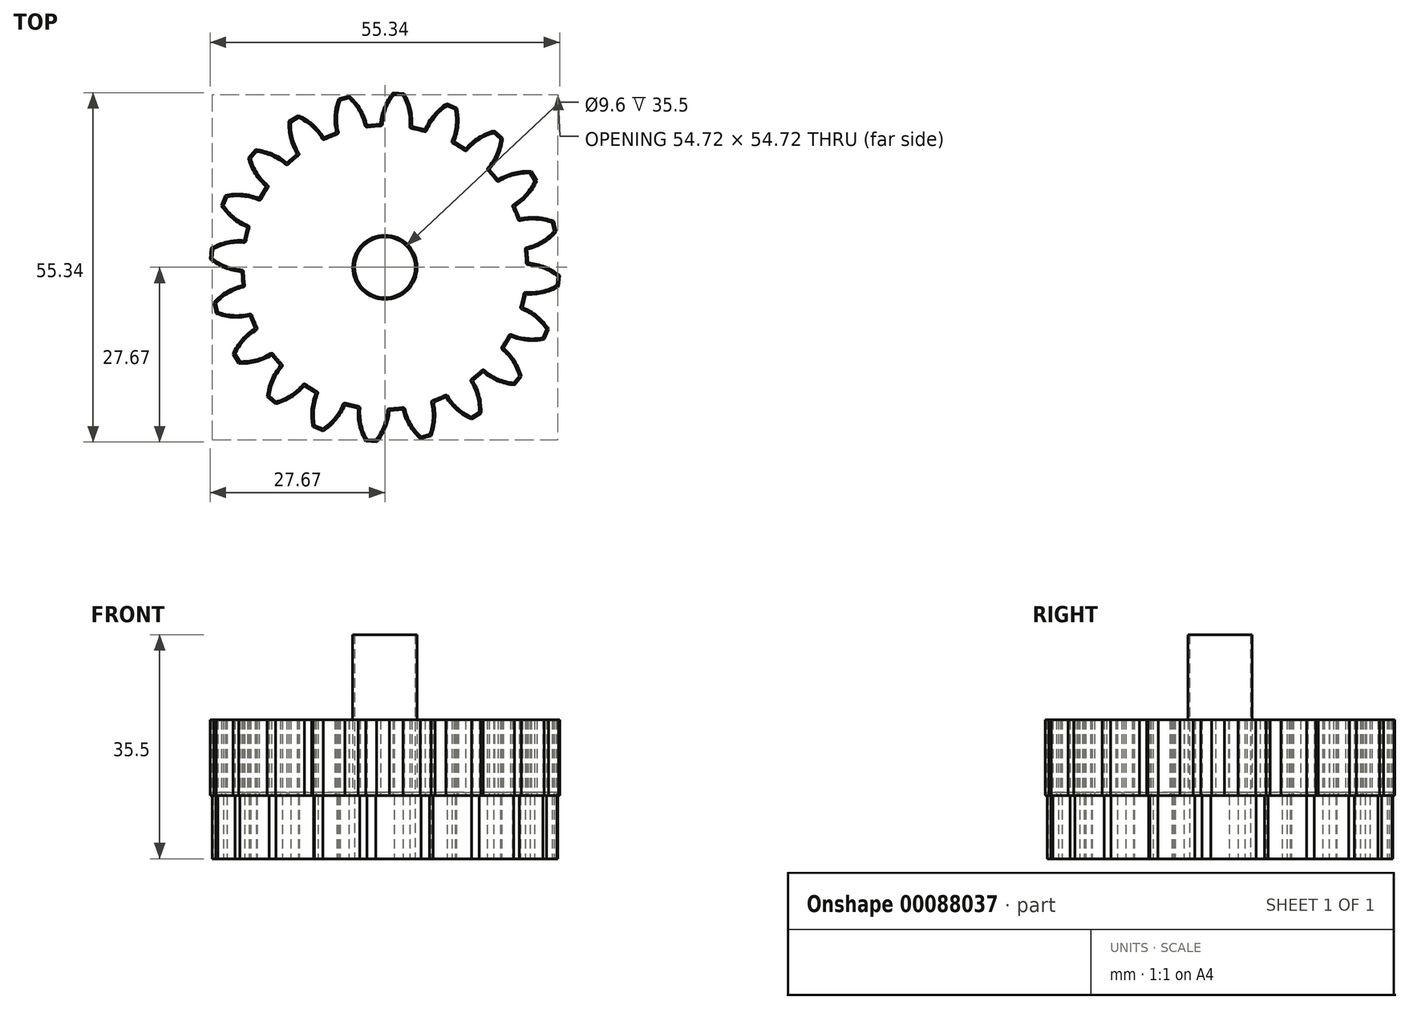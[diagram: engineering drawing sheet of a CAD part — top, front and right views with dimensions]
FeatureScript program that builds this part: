
annotation { "Feature Type Name" : "Feature", "Feature Type Description" : "" }
export const myFeature = defineFeature(function(context is Context, id is Id, definition is map)
    precondition{}
    {
        {
            assignVariable(context, id + "F0", {"name" : "z", "anyValue" : 20});
        }
        {
            assignVariable(context, id + "F1", {"name" : "b1", "anyValue" : 10});
        }
        {
            var Q0;
            Q0=qCreatedBy(makeId("Top.planeOp"),FACE);
            var sketch = newSketch(context, id + "F2", { "sketchPlane" : qUnion([Q0])});
            skCircle(sketch, "E0", {"center": v(0, 0) * mm, "radius": 27.5 * mm, "construction": true});
            skCircle(sketch, "E1", {"center": v(0, 0) * mm, "radius": 23.5 * mm, "construction": true});
            skCircle(sketch, "E2", {"center": v(0, 0) * mm, "radius": 25 * mm, "construction": true});
            skCircle(sketch, "E3", {"center": v(0, 0) * mm, "radius": 22.5 * mm, "construction": true});
            skLineSegment(sketch, "E4", {"start": v(0, 0) * mm, "end": v(9.4, 25.84) * mm, "construction": true});
            skLineSegment(sketch, "E5", {"start": v(0, 27.5) * mm, "end": v(0, 0) * mm, "construction": true});
            skCircle(sketch, "E6", {"center": v(8.03, 22.08) * mm, "radius": 8.55 * mm, "construction": true});
            skPoint(sketch, "E7", {"position": v(0, 25) * mm});
            skLineSegment(sketch, "E8", {"start": v(4.3, 27.16) * mm, "end": v(0, 0) * mm, "construction": true});
            skLineSegment(sketch, "E9", {"start": v(0, 0) * mm, "end": v(-5.25, 27) * mm, "construction": true});
            skCircle(sketch, "E10", {"center": v(-4.48, 23.06) * mm, "radius": 8.55 * mm, "construction": true});
            skPoint(sketch, "E11", {"position": v(3.91, 24.7) * mm});
            skCircle(sketch, "E12", {"center": v(0, 0) * mm, "radius": 22.4 * mm, "construction": true});
            skCircle(sketch, "E13", {"center": v(0, 0) * mm, "radius": 27.4 * mm, "construction": true});
            skCircle(sketch, "E14", {"center": v(-4.48, 23.06) * mm, "radius": 8.45 * mm, "construction": true});
            skCircle(sketch, "E15", {"center": v(8.03, 22.08) * mm, "radius": 8.45 * mm, "construction": true});
            skCircle(sketch, "E16", {"center": v(-0.7, 22.69) * mm, "radius": 0.3 * mm, "construction": true});
            skCircle(sketch, "E17", {"center": v(4.23, 22.3) * mm, "radius": 0.3 * mm, "construction": true});
            skPoint(sketch, "E18", {"position": v(-0.68, 22.39) * mm});
            skPoint(sketch, "E19", {"position": v(-0.4, 22.67) * mm});
            skPoint(sketch, "E20", {"position": v(3.94, 22.33) * mm});
            skPoint(sketch, "E21", {"position": v(4.18, 22) * mm});
            skPoint(sketch, "E22", {"position": v(2.86, 27.25) * mm});
            skPoint(sketch, "E23", {"position": v(1.44, 27.36) * mm});
            skArc(sketch, "E24", {"start": v(-0.68, 22.39) * mm, "mid": v(-0.49, 22.47) * mm, "end": v(-0.4, 22.67) * mm});
            skArc(sketch, "E25", {"start": v(1.44, 27.36) * mm, "mid": v(0.17, 25.16) * mm, "end": v(-0.4, 22.67) * mm});
            skArc(sketch, "E26", {"start": v(3.94, 22.33) * mm, "mid": v(4, 22.12) * mm, "end": v(4.18, 22) * mm});
            skArc(sketch, "E27", {"start": v(3.94, 22.33) * mm, "mid": v(3.77, 24.87) * mm, "end": v(2.86, 27.25) * mm});
            skArc(sketch, "E28", {"start": v(4.18, 22) * mm, "mid": v(1.76, 22.33) * mm, "end": v(-0.68, 22.39) * mm});
            skLineSegment(sketch, "E29", {"start": v(2.86, 27.25) * mm, "end": v(1.44, 27.36) * mm});
            skSolve(sketch);
        }
        {
            var Q0;
            Q0=qSketchRegion(id+"F2",true);
            extrude(context, id + "F3", {"entities" : qUnion([Q0]), "depth" : (getVariable(context, 'b1')) * mm});
        }
        {
            var Q0;
            Q0=qCreatedBy(makeId("Front.planeOp"),FACE);
            var sketch = newSketch(context, id + "F4", { "sketchPlane" : qUnion([Q0])});
            skLineSegment(sketch, "E30", {"start": v(0, 0) * mm, "end": v(0, 15) * mm, "construction": true});
            skSolve(sketch);
        }
        {
            var Q0;
            Q0=makeQuery(id+"F3.opExtrude","SWEPT_BODY",BODY,{"disambiguationData":[OSD([sQuery(id+"F2.wireOp",EDGE,"E24"),sQuery(id+"F2.wireOp",EDGE,"E25"),sQuery(id+"F2.wireOp",EDGE,"E26"),sQuery(id+"F2.wireOp",EDGE,"E27"),sQuery(id+"F2.wireOp",EDGE,"E28"),sQuery(id+"F2.wireOp",EDGE,"debd62c7-c6de-4254-9725-9acab07f6eeb")])]});
            var Q1;
            Q1=sQuery(id+"F4.wireOp",EDGE,"E30");
            circularPattern(context, id + "F5", {"entities" : qUnion([Q0]), "axis" : qUnion([Q1]), "angle" : (360 / getVariable(context, 'z')) * degree, "instanceCount" : getVariable(context, 'z')});
        }
        {
            var Q0;
            Q0=qCreatedBy(makeId("Top.planeOp"),FACE);
            var sketch = newSketch(context, id + "F6", { "sketchPlane" : qUnion([Q0])});
            skCircle(sketch, "E31", {"center": v(0, 0) * mm, "radius": 22.4 * mm});
            skCircle(sketch, "E32", {"center": v(0, 0) * mm, "radius": 4.8 * mm});
            skSolve(sketch);
        }
        {
            var Q0;
            Q0=qSketchRegion(id+"F6",true);
            extrude(context, id + "F7", {"entities" : qUnion([Q0]), "operationType" : NewBodyOperationType.ADD, "depth" : (getVariable(context, 'b1')) * mm});
        }
        {
            var Q0;
            {var subQ0=makeQuery(id+"F3.opExtrude","CAP_FACE",FACE,{"disambiguationData":[OSD([sQuery(id+"F2.wireOp",EDGE,"E24"),sQuery(id+"F2.wireOp",EDGE,"E25"),sQuery(id+"F2.wireOp",EDGE,"E26"),sQuery(id+"F2.wireOp",EDGE,"E27"),sQuery(id+"F2.wireOp",EDGE,"E28"),sQuery(id+"F2.wireOp",EDGE,"E29")])],"isStart":false});Q0=makeQuery(id+"F7.boolean.opBoolean","MERGE",FACE,{"derivedFrom":[subQ0,makeQuery(id+"F5.opPattern","COPY",FACE,{"derivedFrom":subQ0,"instanceName":"1"}),makeQuery(id+"F5.opPattern","COPY",FACE,{"derivedFrom":subQ0,"instanceName":"2"}),makeQuery(id+"F5.opPattern","COPY",FACE,{"derivedFrom":subQ0,"instanceName":"3"}),makeQuery(id+"F5.opPattern","COPY",FACE,{"derivedFrom":subQ0,"instanceName":"4"}),makeQuery(id+"F5.opPattern","COPY",FACE,{"derivedFrom":subQ0,"instanceName":"5"}),makeQuery(id+"F5.opPattern","COPY",FACE,{"derivedFrom":subQ0,"instanceName":"6"}),makeQuery(id+"F5.opPattern","COPY",FACE,{"derivedFrom":subQ0,"instanceName":"7"}),makeQuery(id+"F5.opPattern","COPY",FACE,{"derivedFrom":subQ0,"instanceName":"8"}),makeQuery(id+"F5.opPattern","COPY",FACE,{"derivedFrom":subQ0,"instanceName":"9"}),makeQuery(id+"F5.opPattern","COPY",FACE,{"derivedFrom":subQ0,"instanceName":"10"}),makeQuery(id+"F5.opPattern","COPY",FACE,{"derivedFrom":subQ0,"instanceName":"11"}),makeQuery(id+"F5.opPattern","COPY",FACE,{"derivedFrom":subQ0,"instanceName":"12"}),makeQuery(id+"F5.opPattern","COPY",FACE,{"derivedFrom":subQ0,"instanceName":"13"}),makeQuery(id+"F5.opPattern","COPY",FACE,{"derivedFrom":subQ0,"instanceName":"14"}),makeQuery(id+"F5.opPattern","COPY",FACE,{"derivedFrom":subQ0,"instanceName":"15"}),makeQuery(id+"F5.opPattern","COPY",FACE,{"derivedFrom":subQ0,"instanceName":"16"}),makeQuery(id+"F5.opPattern","COPY",FACE,{"derivedFrom":subQ0,"instanceName":"17"}),makeQuery(id+"F5.opPattern","COPY",FACE,{"derivedFrom":subQ0,"instanceName":"18"}),makeQuery(id+"F5.opPattern","COPY",FACE,{"derivedFrom":subQ0,"instanceName":"19"}),makeQuery(id+"F7.opExtrude","CAP_FACE",FACE,{"disambiguationData":[OSD([sQuery(id+"F6.wireOp",EDGE,"E31"),sQuery(id+"F6.wireOp",EDGE,"E32")])],"isStart":false})]});}
            var sketch = newSketch(context, id + "F8", { "sketchPlane" : qUnion([Q0])});
            skArc(sketch, "E33.0", {"start": v(1.44, 27.36) * mm, "mid": v(0.17, 25.16) * mm, "end": v(-0.4, 22.67) * mm});
            skLineSegment(sketch, "E33.1", {"start": v(2.86, 27.25) * mm, "end": v(1.44, 27.36) * mm});
            skArc(sketch, "E33.2", {"start": v(3.94, 22.33) * mm, "mid": v(3.77, 24.87) * mm, "end": v(2.86, 27.25) * mm});
            skArc(sketch, "E33.3", {"start": v(-0.68, 22.39) * mm, "mid": v(-0.49, 22.47) * mm, "end": v(-0.4, 22.67) * mm});
            skArc(sketch, "E33.4", {"start": v(3.94, 22.33) * mm, "mid": v(4, 22.12) * mm, "end": v(4.18, 22) * mm});
            skArc(sketch, "E33.5", {"start": v(6.27, 21.5) * mm, "mid": v(5.23, 21.78) * mm, "end": v(4.18, 22) * mm});
            skArc(sketch, "E34", {"start": v(1.3, 27.67) * mm, "mid": v(-0.08, 25.34) * mm, "end": v(-0.7, 22.69) * mm});
            skArc(sketch, "E35", {"start": v(4.23, 22.3) * mm, "mid": v(4.05, 25.01) * mm, "end": v(3.04, 27.54) * mm});
            skLineSegment(sketch, "E36", {"start": v(1.3, 27.67) * mm, "end": v(3.04, 27.54) * mm});
            skArc(sketch, "E37.0", {"start": v(6.27, 21.5) * mm, "mid": v(6.48, 21.52) * mm, "end": v(6.63, 21.68) * mm, "construction": true});
            skLineSegment(sketch, "E38", {"start": v(4.23, 22.3) * mm, "end": v(6.35, 21.8) * mm});
            skArc(sketch, "E39.1.0", {"start": v(-2.86, 22.52) * mm, "mid": v(-3.88, 25.04) * mm, "end": v(-5.62, 27.13) * mm});
            skArc(sketch, "E39.1.1", {"start": v(-7.3, 26.72) * mm, "mid": v(-7.91, 24.07) * mm, "end": v(-7.67, 21.36) * mm});
            skArc(sketch, "E39.1.2", {"start": v(-0.68, 22.39) * mm, "mid": v(-1.76, 22.33) * mm, "end": v(-2.83, 22.22) * mm});
            skArc(sketch, "E39.1.3", {"start": v(-3.16, 22.45) * mm, "mid": v(-4.1, 24.82) * mm, "end": v(-5.7, 26.8) * mm});
            skLineSegment(sketch, "E39.1.4", {"start": v(-5.7, 26.8) * mm, "end": v(-7.08, 26.47) * mm});
            skArc(sketch, "E39.1.5", {"start": v(-7.08, 26.47) * mm, "mid": v(-7.62, 23.98) * mm, "end": v(-7.38, 21.44) * mm});
            skLineSegment(sketch, "E39.1.6", {"start": v(-7.3, 26.72) * mm, "end": v(-5.62, 27.13) * mm});
            skLineSegment(sketch, "E39.1.7", {"start": v(-2.86, 22.52) * mm, "end": v(-0.7, 22.69) * mm});
            skArc(sketch, "E39.1.8", {"start": v(-7.57, 21.08) * mm, "mid": v(-7.4, 21.22) * mm, "end": v(-7.38, 21.44) * mm});
            skArc(sketch, "E39.1.9", {"start": v(-3.16, 22.45) * mm, "mid": v(-3.04, 22.27) * mm, "end": v(-2.83, 22.22) * mm});
            skArc(sketch, "E39.2.0", {"start": v(-9.68, 20.53) * mm, "mid": v(-11.43, 22.62) * mm, "end": v(-13.73, 24.06) * mm});
            skArc(sketch, "E39.2.1", {"start": v(-15.2, 23.16) * mm, "mid": v(-14.96, 20.45) * mm, "end": v(-13.9, 17.95) * mm});
            skArc(sketch, "E39.2.2", {"start": v(-7.57, 21.08) * mm, "mid": v(-8.57, 20.7) * mm, "end": v(-9.55, 20.26) * mm});
            skArc(sketch, "E39.2.3", {"start": v(-9.94, 20.38) * mm, "mid": v(-11.57, 22.34) * mm, "end": v(-13.7, 23.73) * mm});
            skLineSegment(sketch, "E39.2.4", {"start": v(-13.7, 23.73) * mm, "end": v(-14.92, 22.98) * mm});
            skArc(sketch, "E39.2.5", {"start": v(-14.92, 22.98) * mm, "mid": v(-14.65, 20.45) * mm, "end": v(-13.64, 18.1) * mm});
            skLineSegment(sketch, "E39.2.6", {"start": v(-15.2, 23.16) * mm, "end": v(-13.73, 24.06) * mm});
            skLineSegment(sketch, "E39.2.7", {"start": v(-9.68, 20.53) * mm, "end": v(-7.67, 21.36) * mm});
            skArc(sketch, "E39.2.8", {"start": v(-13.71, 17.71) * mm, "mid": v(-13.6, 17.9) * mm, "end": v(-13.64, 18.1) * mm});
            skArc(sketch, "E39.2.9", {"start": v(-9.94, 20.38) * mm, "mid": v(-9.77, 20.24) * mm, "end": v(-9.55, 20.26) * mm});
            skArc(sketch, "E39.3.0", {"start": v(-15.55, 16.53) * mm, "mid": v(-17.86, 17.98) * mm, "end": v(-20.5, 18.64) * mm});
            skArc(sketch, "E39.3.1", {"start": v(-21.62, 17.33) * mm, "mid": v(-20.55, 14.83) * mm, "end": v(-18.76, 12.77) * mm});
            skArc(sketch, "E39.3.2", {"start": v(-13.71, 17.71) * mm, "mid": v(-14.55, 17.03) * mm, "end": v(-15.35, 16.32) * mm});
            skArc(sketch, "E39.3.3", {"start": v(-15.75, 16.3) * mm, "mid": v(-17.9, 17.67) * mm, "end": v(-20.37, 18.33) * mm});
            skLineSegment(sketch, "E39.3.4", {"start": v(-20.37, 18.33) * mm, "end": v(-21.29, 17.25) * mm});
            skArc(sketch, "E39.3.5", {"start": v(-21.29, 17.25) * mm, "mid": v(-20.25, 14.92) * mm, "end": v(-18.57, 13) * mm});
            skLineSegment(sketch, "E39.3.6", {"start": v(-21.62, 17.33) * mm, "end": v(-20.5, 18.64) * mm});
            skLineSegment(sketch, "E39.3.7", {"start": v(-15.55, 16.53) * mm, "end": v(-13.9, 17.95) * mm});
            skArc(sketch, "E39.3.8", {"start": v(-18.52, 12.6) * mm, "mid": v(-18.47, 12.82) * mm, "end": v(-18.57, 13) * mm});
            skArc(sketch, "E39.3.9", {"start": v(-15.75, 16.3) * mm, "mid": v(-15.55, 16.23) * mm, "end": v(-15.35, 16.32) * mm});
            skArc(sketch, "E39.4.0", {"start": v(-19.9, 10.92) * mm, "mid": v(-22.54, 11.58) * mm, "end": v(-25.25, 11.4) * mm});
            skArc(sketch, "E39.4.1", {"start": v(-25.91, 9.8) * mm, "mid": v(-24.12, 7.75) * mm, "end": v(-21.8, 6.35) * mm});
            skArc(sketch, "E39.4.2", {"start": v(-18.52, 12.6) * mm, "mid": v(-19.1, 11.7) * mm, "end": v(-19.64, 10.77) * mm});
            skArc(sketch, "E39.4.3", {"start": v(-20.02, 10.64) * mm, "mid": v(-22.49, 11.27) * mm, "end": v(-25.03, 11.14) * mm});
            skLineSegment(sketch, "E39.4.4", {"start": v(-25.03, 11.14) * mm, "end": v(-25.58, 9.83) * mm});
            skArc(sketch, "E39.4.5", {"start": v(-25.58, 9.83) * mm, "mid": v(-23.87, 7.93) * mm, "end": v(-21.68, 6.63) * mm});
            skLineSegment(sketch, "E39.4.6", {"start": v(-25.91, 9.8) * mm, "end": v(-25.25, 11.4) * mm});
            skLineSegment(sketch, "E39.4.7", {"start": v(-19.9, 10.92) * mm, "end": v(-18.76, 12.77) * mm});
            skArc(sketch, "E39.4.8", {"start": v(-21.5, 6.27) * mm, "mid": v(-21.52, 6.48) * mm, "end": v(-21.68, 6.63) * mm});
            skArc(sketch, "E39.4.9", {"start": v(-20.02, 10.64) * mm, "mid": v(-19.8, 10.64) * mm, "end": v(-19.64, 10.77) * mm});
            skArc(sketch, "E39.5.0", {"start": v(-22.3, 4.23) * mm, "mid": v(-25.01, 4.05) * mm, "end": v(-27.54, 3.04) * mm});
            skArc(sketch, "E39.5.1", {"start": v(-27.67, 1.3) * mm, "mid": v(-25.34, -0.08) * mm, "end": v(-22.69, -0.7) * mm});
            skArc(sketch, "E39.5.2", {"start": v(-21.5, 6.27) * mm, "mid": v(-21.78, 5.23) * mm, "end": v(-22, 4.18) * mm});
            skArc(sketch, "E39.5.3", {"start": v(-22.33, 3.94) * mm, "mid": v(-24.87, 3.77) * mm, "end": v(-27.25, 2.86) * mm});
            skLineSegment(sketch, "E39.5.4", {"start": v(-27.25, 2.86) * mm, "end": v(-27.36, 1.44) * mm});
            skArc(sketch, "E39.5.5", {"start": v(-27.36, 1.44) * mm, "mid": v(-25.16, 0.17) * mm, "end": v(-22.67, -0.4) * mm});
            skLineSegment(sketch, "E39.5.6", {"start": v(-27.67, 1.3) * mm, "end": v(-27.54, 3.04) * mm});
            skLineSegment(sketch, "E39.5.7", {"start": v(-22.3, 4.23) * mm, "end": v(-21.8, 6.35) * mm});
            skArc(sketch, "E39.5.8", {"start": v(-22.39, -0.68) * mm, "mid": v(-22.47, -0.49) * mm, "end": v(-22.67, -0.4) * mm});
            skArc(sketch, "E39.5.9", {"start": v(-22.33, 3.94) * mm, "mid": v(-22.12, 4) * mm, "end": v(-22, 4.18) * mm});
            skArc(sketch, "E39.6.0", {"start": v(-22.52, -2.86) * mm, "mid": v(-25.04, -3.88) * mm, "end": v(-27.13, -5.62) * mm});
            skArc(sketch, "E39.6.1", {"start": v(-26.72, -7.3) * mm, "mid": v(-24.07, -7.91) * mm, "end": v(-21.36, -7.67) * mm});
            skArc(sketch, "E39.6.2", {"start": v(-22.39, -0.68) * mm, "mid": v(-22.33, -1.76) * mm, "end": v(-22.22, -2.83) * mm});
            skArc(sketch, "E39.6.3", {"start": v(-22.45, -3.16) * mm, "mid": v(-24.82, -4.1) * mm, "end": v(-26.8, -5.7) * mm});
            skLineSegment(sketch, "E39.6.4", {"start": v(-26.8, -5.7) * mm, "end": v(-26.47, -7.08) * mm});
            skArc(sketch, "E39.6.5", {"start": v(-26.47, -7.08) * mm, "mid": v(-23.98, -7.62) * mm, "end": v(-21.44, -7.38) * mm});
            skLineSegment(sketch, "E39.6.6", {"start": v(-26.72, -7.3) * mm, "end": v(-27.13, -5.62) * mm});
            skLineSegment(sketch, "E39.6.7", {"start": v(-22.52, -2.86) * mm, "end": v(-22.69, -0.7) * mm});
            skArc(sketch, "E39.6.8", {"start": v(-21.08, -7.57) * mm, "mid": v(-21.22, -7.4) * mm, "end": v(-21.44, -7.38) * mm});
            skArc(sketch, "E39.6.9", {"start": v(-22.45, -3.16) * mm, "mid": v(-22.27, -3.04) * mm, "end": v(-22.22, -2.83) * mm});
            skArc(sketch, "E39.7.0", {"start": v(-20.53, -9.68) * mm, "mid": v(-22.62, -11.43) * mm, "end": v(-24.06, -13.73) * mm});
            skArc(sketch, "E39.7.1", {"start": v(-23.16, -15.2) * mm, "mid": v(-20.45, -14.96) * mm, "end": v(-17.95, -13.9) * mm});
            skArc(sketch, "E39.7.2", {"start": v(-21.08, -7.57) * mm, "mid": v(-20.7, -8.57) * mm, "end": v(-20.26, -9.55) * mm});
            skArc(sketch, "E39.7.3", {"start": v(-20.38, -9.94) * mm, "mid": v(-22.34, -11.57) * mm, "end": v(-23.73, -13.7) * mm});
            skLineSegment(sketch, "E39.7.4", {"start": v(-23.73, -13.7) * mm, "end": v(-22.98, -14.92) * mm});
            skArc(sketch, "E39.7.5", {"start": v(-22.98, -14.92) * mm, "mid": v(-20.45, -14.65) * mm, "end": v(-18.1, -13.64) * mm});
            skLineSegment(sketch, "E39.7.6", {"start": v(-23.16, -15.2) * mm, "end": v(-24.06, -13.73) * mm});
            skLineSegment(sketch, "E39.7.7", {"start": v(-20.53, -9.68) * mm, "end": v(-21.36, -7.67) * mm});
            skArc(sketch, "E39.7.8", {"start": v(-17.71, -13.71) * mm, "mid": v(-17.9, -13.6) * mm, "end": v(-18.1, -13.64) * mm});
            skArc(sketch, "E39.7.9", {"start": v(-20.38, -9.94) * mm, "mid": v(-20.24, -9.77) * mm, "end": v(-20.26, -9.55) * mm});
            skArc(sketch, "E39.8.0", {"start": v(-16.53, -15.55) * mm, "mid": v(-17.98, -17.86) * mm, "end": v(-18.64, -20.5) * mm});
            skArc(sketch, "E39.8.1", {"start": v(-17.33, -21.62) * mm, "mid": v(-14.83, -20.55) * mm, "end": v(-12.77, -18.76) * mm});
            skArc(sketch, "E39.8.2", {"start": v(-17.71, -13.71) * mm, "mid": v(-17.03, -14.55) * mm, "end": v(-16.32, -15.35) * mm});
            skArc(sketch, "E39.8.3", {"start": v(-16.3, -15.75) * mm, "mid": v(-17.67, -17.9) * mm, "end": v(-18.33, -20.37) * mm});
            skLineSegment(sketch, "E39.8.4", {"start": v(-18.33, -20.37) * mm, "end": v(-17.25, -21.29) * mm});
            skArc(sketch, "E39.8.5", {"start": v(-17.25, -21.29) * mm, "mid": v(-14.92, -20.25) * mm, "end": v(-13, -18.57) * mm});
            skLineSegment(sketch, "E39.8.6", {"start": v(-17.33, -21.62) * mm, "end": v(-18.64, -20.5) * mm});
            skLineSegment(sketch, "E39.8.7", {"start": v(-16.53, -15.55) * mm, "end": v(-17.95, -13.9) * mm});
            skArc(sketch, "E39.8.8", {"start": v(-12.6, -18.52) * mm, "mid": v(-12.82, -18.47) * mm, "end": v(-13, -18.57) * mm});
            skArc(sketch, "E39.8.9", {"start": v(-16.3, -15.75) * mm, "mid": v(-16.23, -15.55) * mm, "end": v(-16.32, -15.35) * mm});
            skArc(sketch, "E39.9.0", {"start": v(-10.92, -19.9) * mm, "mid": v(-11.58, -22.54) * mm, "end": v(-11.4, -25.25) * mm});
            skArc(sketch, "E39.9.1", {"start": v(-9.8, -25.91) * mm, "mid": v(-7.75, -24.12) * mm, "end": v(-6.35, -21.8) * mm});
            skArc(sketch, "E39.9.2", {"start": v(-12.6, -18.52) * mm, "mid": v(-11.7, -19.1) * mm, "end": v(-10.77, -19.64) * mm});
            skArc(sketch, "E39.9.3", {"start": v(-10.64, -20.02) * mm, "mid": v(-11.27, -22.49) * mm, "end": v(-11.14, -25.03) * mm});
            skLineSegment(sketch, "E39.9.4", {"start": v(-11.14, -25.03) * mm, "end": v(-9.83, -25.58) * mm});
            skArc(sketch, "E39.9.5", {"start": v(-9.83, -25.58) * mm, "mid": v(-7.93, -23.87) * mm, "end": v(-6.63, -21.68) * mm});
            skLineSegment(sketch, "E39.9.6", {"start": v(-9.8, -25.91) * mm, "end": v(-11.4, -25.25) * mm});
            skLineSegment(sketch, "E39.9.7", {"start": v(-10.92, -19.9) * mm, "end": v(-12.77, -18.76) * mm});
            skArc(sketch, "E39.9.8", {"start": v(-6.27, -21.5) * mm, "mid": v(-6.48, -21.52) * mm, "end": v(-6.63, -21.68) * mm});
            skArc(sketch, "E39.9.9", {"start": v(-10.64, -20.02) * mm, "mid": v(-10.64, -19.8) * mm, "end": v(-10.77, -19.64) * mm});
            skArc(sketch, "E39.10.0", {"start": v(-4.23, -22.3) * mm, "mid": v(-4.05, -25.01) * mm, "end": v(-3.04, -27.54) * mm});
            skArc(sketch, "E39.10.1", {"start": v(-1.3, -27.67) * mm, "mid": v(0.08, -25.34) * mm, "end": v(0.7, -22.69) * mm});
            skArc(sketch, "E39.10.2", {"start": v(-6.27, -21.5) * mm, "mid": v(-5.23, -21.78) * mm, "end": v(-4.18, -22) * mm});
            skArc(sketch, "E39.10.3", {"start": v(-3.94, -22.33) * mm, "mid": v(-3.77, -24.87) * mm, "end": v(-2.86, -27.25) * mm});
            skLineSegment(sketch, "E39.10.4", {"start": v(-2.86, -27.25) * mm, "end": v(-1.44, -27.36) * mm});
            skArc(sketch, "E39.10.5", {"start": v(-1.44, -27.36) * mm, "mid": v(-0.17, -25.16) * mm, "end": v(0.4, -22.67) * mm});
            skLineSegment(sketch, "E39.10.6", {"start": v(-1.3, -27.67) * mm, "end": v(-3.04, -27.54) * mm});
            skLineSegment(sketch, "E39.10.7", {"start": v(-4.23, -22.3) * mm, "end": v(-6.35, -21.8) * mm});
            skArc(sketch, "E39.10.8", {"start": v(0.68, -22.39) * mm, "mid": v(0.49, -22.47) * mm, "end": v(0.4, -22.67) * mm});
            skArc(sketch, "E39.10.9", {"start": v(-3.94, -22.33) * mm, "mid": v(-4, -22.12) * mm, "end": v(-4.18, -22) * mm});
            skArc(sketch, "E39.11.0", {"start": v(2.86, -22.52) * mm, "mid": v(3.88, -25.04) * mm, "end": v(5.62, -27.13) * mm});
            skArc(sketch, "E39.11.1", {"start": v(7.3, -26.72) * mm, "mid": v(7.91, -24.07) * mm, "end": v(7.67, -21.36) * mm});
            skArc(sketch, "E39.11.2", {"start": v(0.68, -22.39) * mm, "mid": v(1.76, -22.33) * mm, "end": v(2.83, -22.22) * mm});
            skArc(sketch, "E39.11.3", {"start": v(3.16, -22.45) * mm, "mid": v(4.1, -24.82) * mm, "end": v(5.7, -26.8) * mm});
            skLineSegment(sketch, "E39.11.4", {"start": v(5.7, -26.8) * mm, "end": v(7.08, -26.47) * mm});
            skArc(sketch, "E39.11.5", {"start": v(7.08, -26.47) * mm, "mid": v(7.62, -23.98) * mm, "end": v(7.38, -21.44) * mm});
            skLineSegment(sketch, "E39.11.6", {"start": v(7.3, -26.72) * mm, "end": v(5.62, -27.13) * mm});
            skLineSegment(sketch, "E39.11.7", {"start": v(2.86, -22.52) * mm, "end": v(0.7, -22.69) * mm});
            skArc(sketch, "E39.11.8", {"start": v(7.57, -21.08) * mm, "mid": v(7.4, -21.22) * mm, "end": v(7.38, -21.44) * mm});
            skArc(sketch, "E39.11.9", {"start": v(3.16, -22.45) * mm, "mid": v(3.04, -22.27) * mm, "end": v(2.83, -22.22) * mm});
            skArc(sketch, "E39.12.0", {"start": v(9.68, -20.53) * mm, "mid": v(11.43, -22.62) * mm, "end": v(13.73, -24.06) * mm});
            skArc(sketch, "E39.12.1", {"start": v(15.2, -23.16) * mm, "mid": v(14.96, -20.45) * mm, "end": v(13.9, -17.95) * mm});
            skArc(sketch, "E39.12.2", {"start": v(7.57, -21.08) * mm, "mid": v(8.57, -20.7) * mm, "end": v(9.55, -20.26) * mm});
            skArc(sketch, "E39.12.3", {"start": v(9.94, -20.38) * mm, "mid": v(11.57, -22.34) * mm, "end": v(13.7, -23.73) * mm});
            skLineSegment(sketch, "E39.12.4", {"start": v(13.7, -23.73) * mm, "end": v(14.92, -22.98) * mm});
            skArc(sketch, "E39.12.5", {"start": v(14.92, -22.98) * mm, "mid": v(14.65, -20.45) * mm, "end": v(13.64, -18.1) * mm});
            skLineSegment(sketch, "E39.12.6", {"start": v(15.2, -23.16) * mm, "end": v(13.73, -24.06) * mm});
            skLineSegment(sketch, "E39.12.7", {"start": v(9.68, -20.53) * mm, "end": v(7.67, -21.36) * mm});
            skArc(sketch, "E39.12.8", {"start": v(13.71, -17.71) * mm, "mid": v(13.6, -17.9) * mm, "end": v(13.64, -18.1) * mm});
            skArc(sketch, "E39.12.9", {"start": v(9.94, -20.38) * mm, "mid": v(9.77, -20.24) * mm, "end": v(9.55, -20.26) * mm});
            skArc(sketch, "E39.13.0", {"start": v(15.55, -16.53) * mm, "mid": v(17.86, -17.98) * mm, "end": v(20.5, -18.64) * mm});
            skArc(sketch, "E39.13.1", {"start": v(21.62, -17.33) * mm, "mid": v(20.55, -14.83) * mm, "end": v(18.76, -12.77) * mm});
            skArc(sketch, "E39.13.2", {"start": v(13.71, -17.71) * mm, "mid": v(14.55, -17.03) * mm, "end": v(15.35, -16.32) * mm});
            skArc(sketch, "E39.13.3", {"start": v(15.75, -16.3) * mm, "mid": v(17.9, -17.67) * mm, "end": v(20.37, -18.33) * mm});
            skLineSegment(sketch, "E39.13.4", {"start": v(20.37, -18.33) * mm, "end": v(21.29, -17.25) * mm});
            skArc(sketch, "E39.13.5", {"start": v(21.29, -17.25) * mm, "mid": v(20.25, -14.92) * mm, "end": v(18.57, -13) * mm});
            skLineSegment(sketch, "E39.13.6", {"start": v(21.62, -17.33) * mm, "end": v(20.5, -18.64) * mm});
            skLineSegment(sketch, "E39.13.7", {"start": v(15.55, -16.53) * mm, "end": v(13.9, -17.95) * mm});
            skArc(sketch, "E39.13.8", {"start": v(18.52, -12.6) * mm, "mid": v(18.47, -12.82) * mm, "end": v(18.57, -13) * mm});
            skArc(sketch, "E39.13.9", {"start": v(15.75, -16.3) * mm, "mid": v(15.55, -16.23) * mm, "end": v(15.35, -16.32) * mm});
            skArc(sketch, "E39.14.0", {"start": v(19.9, -10.92) * mm, "mid": v(22.54, -11.58) * mm, "end": v(25.25, -11.4) * mm});
            skArc(sketch, "E39.14.1", {"start": v(25.91, -9.8) * mm, "mid": v(24.12, -7.75) * mm, "end": v(21.8, -6.35) * mm});
            skArc(sketch, "E39.14.2", {"start": v(18.52, -12.6) * mm, "mid": v(19.1, -11.7) * mm, "end": v(19.64, -10.77) * mm});
            skArc(sketch, "E39.14.3", {"start": v(20.02, -10.64) * mm, "mid": v(22.49, -11.27) * mm, "end": v(25.03, -11.14) * mm});
            skLineSegment(sketch, "E39.14.4", {"start": v(25.03, -11.14) * mm, "end": v(25.58, -9.83) * mm});
            skArc(sketch, "E39.14.5", {"start": v(25.58, -9.83) * mm, "mid": v(23.87, -7.93) * mm, "end": v(21.68, -6.63) * mm});
            skLineSegment(sketch, "E39.14.6", {"start": v(25.91, -9.8) * mm, "end": v(25.25, -11.4) * mm});
            skLineSegment(sketch, "E39.14.7", {"start": v(19.9, -10.92) * mm, "end": v(18.76, -12.77) * mm});
            skArc(sketch, "E39.14.8", {"start": v(21.5, -6.27) * mm, "mid": v(21.52, -6.48) * mm, "end": v(21.68, -6.63) * mm});
            skArc(sketch, "E39.14.9", {"start": v(20.02, -10.64) * mm, "mid": v(19.8, -10.64) * mm, "end": v(19.64, -10.77) * mm});
            skArc(sketch, "E39.15.0", {"start": v(22.3, -4.23) * mm, "mid": v(25.01, -4.05) * mm, "end": v(27.54, -3.04) * mm});
            skArc(sketch, "E39.15.1", {"start": v(27.67, -1.3) * mm, "mid": v(25.34, 0.08) * mm, "end": v(22.69, 0.7) * mm});
            skArc(sketch, "E39.15.2", {"start": v(21.5, -6.27) * mm, "mid": v(21.78, -5.23) * mm, "end": v(22, -4.18) * mm});
            skArc(sketch, "E39.15.3", {"start": v(22.33, -3.94) * mm, "mid": v(24.87, -3.77) * mm, "end": v(27.25, -2.86) * mm});
            skLineSegment(sketch, "E39.15.4", {"start": v(27.25, -2.86) * mm, "end": v(27.36, -1.44) * mm});
            skArc(sketch, "E39.15.5", {"start": v(27.36, -1.44) * mm, "mid": v(25.16, -0.17) * mm, "end": v(22.67, 0.4) * mm});
            skLineSegment(sketch, "E39.15.6", {"start": v(27.67, -1.3) * mm, "end": v(27.54, -3.04) * mm});
            skLineSegment(sketch, "E39.15.7", {"start": v(22.3, -4.23) * mm, "end": v(21.8, -6.35) * mm});
            skArc(sketch, "E39.15.8", {"start": v(22.39, 0.68) * mm, "mid": v(22.47, 0.49) * mm, "end": v(22.67, 0.4) * mm});
            skArc(sketch, "E39.15.9", {"start": v(22.33, -3.94) * mm, "mid": v(22.12, -4) * mm, "end": v(22, -4.18) * mm});
            skArc(sketch, "E39.16.0", {"start": v(22.52, 2.86) * mm, "mid": v(25.04, 3.88) * mm, "end": v(27.13, 5.62) * mm});
            skArc(sketch, "E39.16.1", {"start": v(26.72, 7.3) * mm, "mid": v(24.07, 7.91) * mm, "end": v(21.36, 7.67) * mm});
            skArc(sketch, "E39.16.2", {"start": v(22.39, 0.68) * mm, "mid": v(22.33, 1.76) * mm, "end": v(22.22, 2.83) * mm});
            skArc(sketch, "E39.16.3", {"start": v(22.45, 3.16) * mm, "mid": v(24.82, 4.1) * mm, "end": v(26.8, 5.7) * mm});
            skLineSegment(sketch, "E39.16.4", {"start": v(26.8, 5.7) * mm, "end": v(26.47, 7.08) * mm});
            skArc(sketch, "E39.16.5", {"start": v(26.47, 7.08) * mm, "mid": v(23.98, 7.62) * mm, "end": v(21.44, 7.38) * mm});
            skLineSegment(sketch, "E39.16.6", {"start": v(26.72, 7.3) * mm, "end": v(27.13, 5.62) * mm});
            skLineSegment(sketch, "E39.16.7", {"start": v(22.52, 2.86) * mm, "end": v(22.69, 0.7) * mm});
            skArc(sketch, "E39.16.8", {"start": v(21.08, 7.57) * mm, "mid": v(21.22, 7.4) * mm, "end": v(21.44, 7.38) * mm});
            skArc(sketch, "E39.16.9", {"start": v(22.45, 3.16) * mm, "mid": v(22.27, 3.04) * mm, "end": v(22.22, 2.83) * mm});
            skArc(sketch, "E39.17.0", {"start": v(20.53, 9.68) * mm, "mid": v(22.62, 11.43) * mm, "end": v(24.06, 13.73) * mm});
            skArc(sketch, "E39.17.1", {"start": v(23.16, 15.2) * mm, "mid": v(20.45, 14.96) * mm, "end": v(17.95, 13.9) * mm});
            skArc(sketch, "E39.17.2", {"start": v(21.08, 7.57) * mm, "mid": v(20.7, 8.57) * mm, "end": v(20.26, 9.55) * mm});
            skArc(sketch, "E39.17.3", {"start": v(20.38, 9.94) * mm, "mid": v(22.34, 11.57) * mm, "end": v(23.73, 13.7) * mm});
            skLineSegment(sketch, "E39.17.4", {"start": v(23.73, 13.7) * mm, "end": v(22.98, 14.92) * mm});
            skArc(sketch, "E39.17.5", {"start": v(22.98, 14.92) * mm, "mid": v(20.45, 14.65) * mm, "end": v(18.1, 13.64) * mm});
            skLineSegment(sketch, "E39.17.6", {"start": v(23.16, 15.2) * mm, "end": v(24.06, 13.73) * mm});
            skLineSegment(sketch, "E39.17.7", {"start": v(20.53, 9.68) * mm, "end": v(21.36, 7.67) * mm});
            skArc(sketch, "E39.17.8", {"start": v(17.71, 13.71) * mm, "mid": v(17.9, 13.6) * mm, "end": v(18.1, 13.64) * mm});
            skArc(sketch, "E39.17.9", {"start": v(20.38, 9.94) * mm, "mid": v(20.24, 9.77) * mm, "end": v(20.26, 9.55) * mm});
            skArc(sketch, "E39.18.0", {"start": v(16.53, 15.55) * mm, "mid": v(17.98, 17.86) * mm, "end": v(18.64, 20.5) * mm});
            skArc(sketch, "E39.18.1", {"start": v(17.33, 21.62) * mm, "mid": v(14.83, 20.55) * mm, "end": v(12.77, 18.76) * mm});
            skArc(sketch, "E39.18.2", {"start": v(17.71, 13.71) * mm, "mid": v(17.03, 14.55) * mm, "end": v(16.32, 15.35) * mm});
            skArc(sketch, "E39.18.3", {"start": v(16.3, 15.75) * mm, "mid": v(17.67, 17.9) * mm, "end": v(18.33, 20.37) * mm});
            skLineSegment(sketch, "E39.18.4", {"start": v(18.33, 20.37) * mm, "end": v(17.25, 21.29) * mm});
            skArc(sketch, "E39.18.5", {"start": v(17.25, 21.29) * mm, "mid": v(14.92, 20.25) * mm, "end": v(13, 18.57) * mm});
            skLineSegment(sketch, "E39.18.6", {"start": v(17.33, 21.62) * mm, "end": v(18.64, 20.5) * mm});
            skLineSegment(sketch, "E39.18.7", {"start": v(16.53, 15.55) * mm, "end": v(17.95, 13.9) * mm});
            skArc(sketch, "E39.18.8", {"start": v(12.6, 18.52) * mm, "mid": v(12.82, 18.47) * mm, "end": v(13, 18.57) * mm});
            skArc(sketch, "E39.18.9", {"start": v(16.3, 15.75) * mm, "mid": v(16.23, 15.55) * mm, "end": v(16.32, 15.35) * mm});
            skArc(sketch, "E39.19.0", {"start": v(10.92, 19.9) * mm, "mid": v(11.58, 22.54) * mm, "end": v(11.4, 25.25) * mm});
            skArc(sketch, "E39.19.1", {"start": v(9.8, 25.91) * mm, "mid": v(7.75, 24.12) * mm, "end": v(6.35, 21.8) * mm});
            skArc(sketch, "E39.19.2", {"start": v(12.6, 18.52) * mm, "mid": v(11.7, 19.1) * mm, "end": v(10.77, 19.64) * mm});
            skArc(sketch, "E39.19.3", {"start": v(10.64, 20.02) * mm, "mid": v(11.27, 22.49) * mm, "end": v(11.14, 25.03) * mm});
            skLineSegment(sketch, "E39.19.4", {"start": v(11.14, 25.03) * mm, "end": v(9.83, 25.58) * mm});
            skArc(sketch, "E39.19.5", {"start": v(9.83, 25.58) * mm, "mid": v(7.93, 23.87) * mm, "end": v(6.63, 21.68) * mm});
            skLineSegment(sketch, "E39.19.6", {"start": v(9.8, 25.91) * mm, "end": v(11.4, 25.25) * mm});
            skLineSegment(sketch, "E39.19.7", {"start": v(10.92, 19.9) * mm, "end": v(12.77, 18.76) * mm});
            skArc(sketch, "E39.19.8", {"start": v(6.27, 21.5) * mm, "mid": v(6.48, 21.52) * mm, "end": v(6.63, 21.68) * mm});
            skArc(sketch, "E39.19.9", {"start": v(10.64, 20.02) * mm, "mid": v(10.64, 19.8) * mm, "end": v(10.77, 19.64) * mm});
            skSolve(sketch);
        }
        {
            var Q0;
            Q0=makeQuery(id+"F8.imprint","IMPRINT",FACE,{"disambiguationData":[TD([[makeQuery(id+"F8.imprint","IMPRINT",EDGE,{"derivedFrom":sQuery(id+"F8.wireOp",EDGE,"E33.0")}),-1.0]])]});
            extrude(context, id + "F9", {"entities" : qUnion([Q0]), "depth" : 12 * mm});
        }
        {
            var Q0;
            {var subQ0=makeQuery(id+"F3.opExtrude","CAP_FACE",FACE,{"disambiguationData":[OSD([sQuery(id+"F2.wireOp",EDGE,"E24"),sQuery(id+"F2.wireOp",EDGE,"E25"),sQuery(id+"F2.wireOp",EDGE,"E26"),sQuery(id+"F2.wireOp",EDGE,"E27"),sQuery(id+"F2.wireOp",EDGE,"E28"),sQuery(id+"F2.wireOp",EDGE,"E29")])],"isStart":false});Q0=makeQuery(id+"F7.boolean.opBoolean","MERGE",FACE,{"derivedFrom":[subQ0,makeQuery(id+"F5.opPattern","COPY",FACE,{"derivedFrom":subQ0,"instanceName":"1"}),makeQuery(id+"F5.opPattern","COPY",FACE,{"derivedFrom":subQ0,"instanceName":"2"}),makeQuery(id+"F5.opPattern","COPY",FACE,{"derivedFrom":subQ0,"instanceName":"3"}),makeQuery(id+"F5.opPattern","COPY",FACE,{"derivedFrom":subQ0,"instanceName":"4"}),makeQuery(id+"F5.opPattern","COPY",FACE,{"derivedFrom":subQ0,"instanceName":"5"}),makeQuery(id+"F5.opPattern","COPY",FACE,{"derivedFrom":subQ0,"instanceName":"6"}),makeQuery(id+"F5.opPattern","COPY",FACE,{"derivedFrom":subQ0,"instanceName":"7"}),makeQuery(id+"F5.opPattern","COPY",FACE,{"derivedFrom":subQ0,"instanceName":"8"}),makeQuery(id+"F5.opPattern","COPY",FACE,{"derivedFrom":subQ0,"instanceName":"9"}),makeQuery(id+"F5.opPattern","COPY",FACE,{"derivedFrom":subQ0,"instanceName":"10"}),makeQuery(id+"F5.opPattern","COPY",FACE,{"derivedFrom":subQ0,"instanceName":"11"}),makeQuery(id+"F5.opPattern","COPY",FACE,{"derivedFrom":subQ0,"instanceName":"12"}),makeQuery(id+"F5.opPattern","COPY",FACE,{"derivedFrom":subQ0,"instanceName":"13"}),makeQuery(id+"F5.opPattern","COPY",FACE,{"derivedFrom":subQ0,"instanceName":"14"}),makeQuery(id+"F5.opPattern","COPY",FACE,{"derivedFrom":subQ0,"instanceName":"15"}),makeQuery(id+"F5.opPattern","COPY",FACE,{"derivedFrom":subQ0,"instanceName":"16"}),makeQuery(id+"F5.opPattern","COPY",FACE,{"derivedFrom":subQ0,"instanceName":"17"}),makeQuery(id+"F5.opPattern","COPY",FACE,{"derivedFrom":subQ0,"instanceName":"18"}),makeQuery(id+"F5.opPattern","COPY",FACE,{"derivedFrom":subQ0,"instanceName":"19"}),makeQuery(id+"F7.opExtrude","CAP_FACE",FACE,{"disambiguationData":[OSD([sQuery(id+"F6.wireOp",EDGE,"E31"),sQuery(id+"F6.wireOp",EDGE,"E32")])],"isStart":false})]});}
            extrude(context, id + "F10", {"entities" : qUnion([Q0]), "operationType" : NewBodyOperationType.ADD, "depth" : 0.5 * mm});
        }
        {
            var Q0;
            Q0=makeQuery(id+"F10.opExtrude","CAP_FACE",FACE,{"disambiguationData":[OSD([sQuery(id+"F2.wireOp",EDGE,"E24"),sQuery(id+"F2.wireOp",EDGE,"E25"),sQuery(id+"F2.wireOp",EDGE,"E26"),sQuery(id+"F2.wireOp",EDGE,"E27"),sQuery(id+"F2.wireOp",EDGE,"E28"),sQuery(id+"F2.wireOp",EDGE,"E29"),sQuery(id+"F6.wireOp",EDGE,"E31"),sQuery(id+"F6.wireOp",EDGE,"E32")])],"isStart":false});
            var sketch = newSketch(context, id + "F11", { "sketchPlane" : qUnion([Q0])});
            skCircle(sketch, "E40.0", {"center": v(0, 0) * mm, "radius": 4.8 * mm});
            skCircle(sketch, "E41", {"center": v(0, 0) * mm, "radius": 5.1 * mm});
            skSolve(sketch);
        }
        {
            var Q0;
            Q0 = qSketchRegion(id + "F11", true);
            extrude(context, id + "F12", {"entities" : qUnion([Q0]), "operationType" : NewBodyOperationType.ADD, "depth" : 25 * mm});
        }
    });
